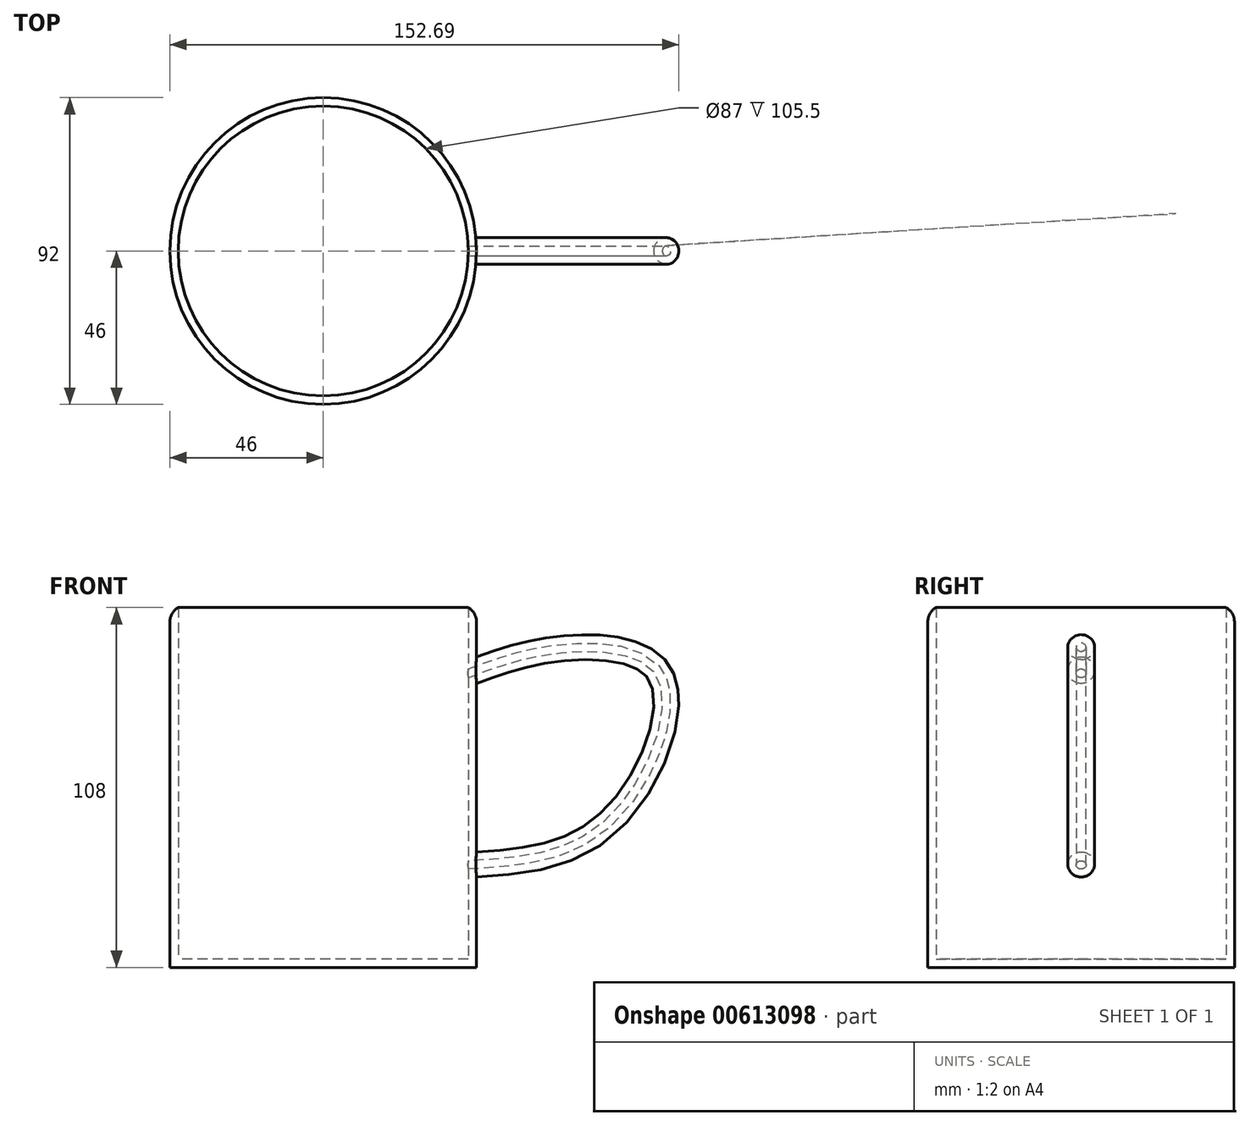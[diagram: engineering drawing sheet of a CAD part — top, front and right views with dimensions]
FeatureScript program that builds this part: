
annotation { "Feature Type Name" : "Feature", "Feature Type Description" : "" }
export const myFeature = defineFeature(function(context is Context, id is Id, definition is map)
    precondition{}
    {
        {
            var Q0;
            Q0=qCreatedBy(makeId("Top.planeOp"),FACE);
            var sketch = newSketch(context, id + "F0", { "sketchPlane" : qUnion([Q0])});
            skCircle(sketch, "E0", {"center": v(0, 0) * mm, "radius": 46 * mm});
            skSolve(sketch);
        }
        {
            var Q0;
            Q0 = qSketchRegion(id + "F0", true);
            extrude(context, id + "F1", {"entities" : qUnion([Q0]), "depth" : 108 * mm, "offsetDistance" : 25 * mm});
        }
        {
            var Q0;
            Q0=qCreatedBy(makeId("Front.planeOp"),FACE);
            var sketch = newSketch(context, id + "F2", { "sketchPlane" : qUnion([Q0])});
            skFitSpline(sketch, "E1", {"points": [v(42.13, 88.41) * mm, v(70.18, 96.18) * mm, v(101.73, 87.91) * mm, v(86.2, 43.1) * mm, v(42.39, 30.07) * mm], "startDerivative": vector(116.12, 44.42) * mm, "endDerivative": vector(-173.3, -9.06) * mm});
            skSolve(sketch);
        }
        {
            var Q0;
            Q0=qCreatedBy(makeId("Right.planeOp"),FACE);
            cPlane(context, id + "F3", {"entities" : qUnion([Q0]), "cplaneType" : CPlaneType.OFFSET, "offset" : 46 * mm, "width" : 150 * mm, "height" : 150 * mm});
        }
        {
            var Q0;
            Q0=qCreatedBy(id+"F3.planeOp",FACE);
            var sketch = newSketch(context, id + "F4", { "sketchPlane" : qUnion([Q0])});
            skCircle(sketch, "E2", {"center": v(0, 89.2) * mm, "radius": 4 * mm});
            skSolve(sketch);
        }
        {
            var Q0;
            Q0=makeQuery(id+"F4.imprint","IMPRINT",FACE,{"disambiguationData":[TD([[makeQuery(id+"F4.imprint","IMPRINT",EDGE,{"derivedFrom":sQuery(id+"F4.wireOp",EDGE,"E2")}),1.0]])]});
            var Q1;
            Q1=sQuery(id+"F2.wireOp",EDGE,"E1");
            sweep(context, id + "F5", {"operationType" : NewBodyOperationType.ADD, "profiles" : qUnion([Q0]), "path" : qUnion([Q1])});
        }
        {
            var Q0;
            Q0=makeQuery(id+"F1.opExtrude","CAP_FACE",FACE,{"disambiguationData":[OSD([sQuery(id+"F0.wireOp",EDGE,"E0")])],"isStart":false});
            shell(context, id + "F6", {"entities" : qUnion([Q0]), "thickness" : 2.5 * mm});
        }
        {
            var Q0;
            Q0=makeQuery(id+"F1.opExtrude","CAP_EDGE",EDGE,{"disambiguationData":[OSD([sQuery(id+"F0.wireOp",EDGE,"E0")])],"isStart":false});
            fillet(context, id + "F7", {"entities" : qUnion([Q0]), "radius" : 5 * mm, "tangentPropagation" : true, "allowEdgeOverflow" : false});
        }
    });
